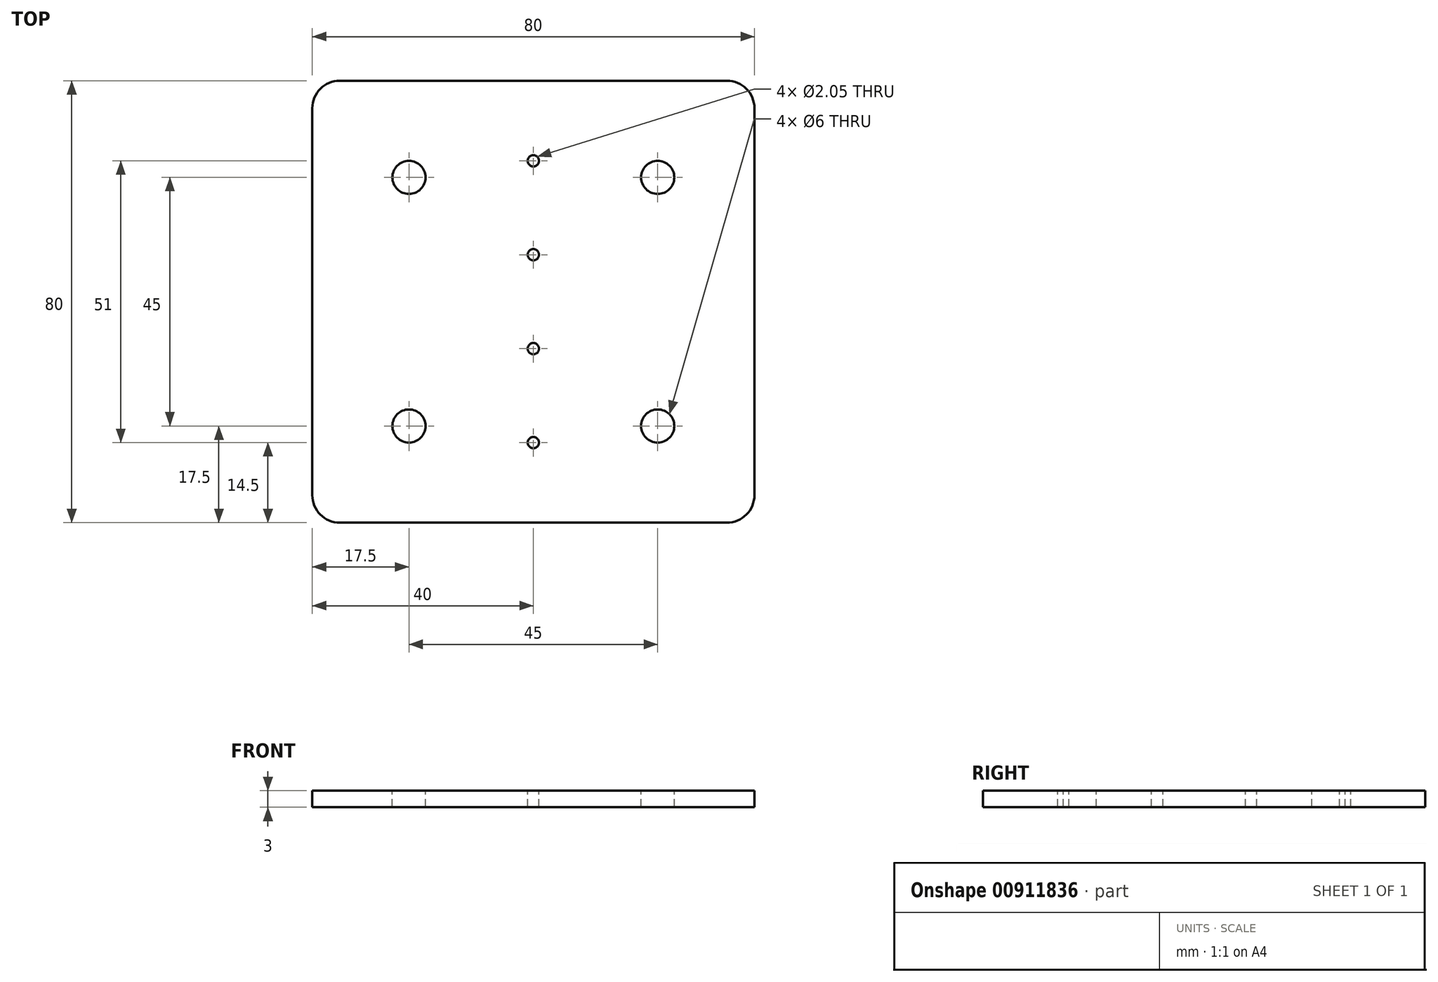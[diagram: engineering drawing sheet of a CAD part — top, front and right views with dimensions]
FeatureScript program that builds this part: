
annotation { "Feature Type Name" : "Feature", "Feature Type Description" : "" }
export const myFeature = defineFeature(function(context is Context, id is Id, definition is map)
    precondition{}
    {
        {
            var Q0;
            Q0=qCreatedBy(makeId("Top.planeOp"),FACE);
            var sketch = newSketch(context, id + "F0", { "sketchPlane" : qUnion([Q0])});
            skLineSegment(sketch, "E0.bottom", {"start": v(5, 0) * mm, "end": v(75, 0) * mm});
            skLineSegment(sketch, "E0.top", {"start": v(5, 80) * mm, "end": v(75, 80) * mm});
            skLineSegment(sketch, "E0.left", {"start": v(0, 5) * mm, "end": v(0, 75) * mm});
            skLineSegment(sketch, "E0.right", {"start": v(80, 5) * mm, "end": v(80, 75) * mm});
            skPoint(sketch, "E1.visualSharp", {"position": v(0, 80) * mm});
            skArc(sketch, "E1.filletArc", {"start": v(5, 80) * mm, "mid": v(1.46, 78.54) * mm, "end": v(0, 75) * mm});
            skPoint(sketch, "E2.visualSharp", {"position": v(80, 80) * mm});
            skArc(sketch, "E2.filletArc", {"start": v(80, 75) * mm, "mid": v(78.54, 78.54) * mm, "end": v(75, 80) * mm});
            skPoint(sketch, "E3.visualSharp", {"position": v(80, 0) * mm});
            skArc(sketch, "E3.filletArc", {"start": v(75, 0) * mm, "mid": v(78.54, 1.46) * mm, "end": v(80, 5) * mm});
            skPoint(sketch, "E4.visualSharp", {"position": v(0, 0) * mm});
            skArc(sketch, "E4.filletArc", {"start": v(0, 5) * mm, "mid": v(1.46, 1.46) * mm, "end": v(5, 0) * mm});
            skSolve(sketch);
        }
        {
            var Q0;
            Q0=makeQuery(id+"F0.imprint","IMPRINT",FACE,{"disambiguationData":[TD([[makeQuery(id+"F0.imprint","IMPRINT",EDGE,{"derivedFrom":sQuery(id+"F0.wireOp",EDGE,"E0.bottom")}),1.0]])]});
            extrude(context, id + "F1", {"entities" : qUnion([Q0]), "depth" : 3 * mm, "offsetDistance" : 25 * mm});
        }
        {
            var Q0;
            Q0=makeQuery(id+"F1.opExtrude","CAP_FACE",FACE,{"disambiguationData":[OSD([sQuery(id+"F0.wireOp",EDGE,"E0.bottom"),sQuery(id+"F0.wireOp",EDGE,"E0.top"),sQuery(id+"F0.wireOp",EDGE,"E0.left"),sQuery(id+"F0.wireOp",EDGE,"E0.right"),sQuery(id+"F0.wireOp",EDGE,"E1.filletArc"),sQuery(id+"F0.wireOp",EDGE,"E2.filletArc"),sQuery(id+"F0.wireOp",EDGE,"E3.filletArc"),sQuery(id+"F0.wireOp",EDGE,"E4.filletArc")])],"isStart":false});
            var sketch = newSketch(context, id + "F2", { "sketchPlane" : qUnion([Q0])});
            skLineSegment(sketch, "E5", {"start": v(40, 80) * mm, "end": v(40, 0) * mm, "construction": true});
            skLineSegment(sketch, "E6", {"start": v(0, 40) * mm, "end": v(80, 40) * mm, "construction": true});
            skCircle(sketch, "E7", {"center": v(40, 48.5) * mm, "radius": 1.02 * mm});
            skCircle(sketch, "E8", {"center": v(40, 31.5) * mm, "radius": 1.02 * mm});
            skCircle(sketch, "E9", {"center": v(62.5, 62.5) * mm, "radius": 3 * mm});
            skCircle(sketch, "E10", {"center": v(40, 65.5) * mm, "radius": 1.02 * mm});
            skCircle(sketch, "E11", {"center": v(40, 14.5) * mm, "radius": 1.02 * mm});
            skCircle(sketch, "E12.0.1.0", {"center": v(62.5, 17.5) * mm, "radius": 3 * mm});
            skCircle(sketch, "E12.1.0.0", {"center": v(17.5, 62.5) * mm, "radius": 3 * mm});
            skCircle(sketch, "E12.1.1.0", {"center": v(17.5, 17.5) * mm, "radius": 3 * mm});
            skLineSegment(sketch, "E12.direction1", {"start": v(62.5, 62.5) * mm, "end": v(17.5, 62.5) * mm, "construction": true});
            skLineSegment(sketch, "E12.direction2", {"start": v(62.5, 62.5) * mm, "end": v(62.5, 17.5) * mm, "construction": true});
            skSolve(sketch);
        }
        {
            var Q0;
            Q0 = qSketchRegion(id + "F2", true);
            extrude(context, id + "F3", {"entities" : qUnion([Q0]), "operationType" : NewBodyOperationType.REMOVE, "oppositeDirection" : true, "depth" : 25 * mm, "offsetDistance" : 25 * mm});
        }
    });
